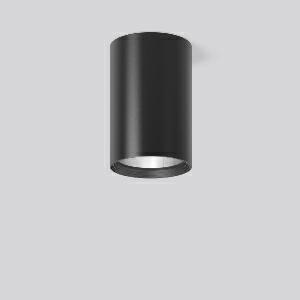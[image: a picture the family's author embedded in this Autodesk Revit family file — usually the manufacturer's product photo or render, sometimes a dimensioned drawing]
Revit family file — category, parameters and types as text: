
# Revit family: heledon_maxi_a_931223_003_76_2b7d
name_source: partatom
category: Lighting Fixtures
units: mm (PartAtom-declared; Revit-internal decimal feet)

## family parameters
Cut with Voids When Loaded = No
Host = Face
Light Source = No
Part Type = Normal
Room Calculation Point = No
Round Connector Dimension = Use Diameter
Shared = No

## types (1)
- HELEDON maxi A (1 x LED Modul 930, 4200 lm, 3000)
    Apparent Load = 35 VA
    Approval mark = CE
    CIE Flux Codes = 100 100 100 100 100
    Color Rendering = 90
    Color Temperature = 3000
    Default Elevation = 1800 mm
    Description = Series: HELEDON maxi
Cylindrical surface-mounted downlight. Housing: die-cast aluminium, powder-coated. Internal ceiling frame polycarbonate with bayonet mounting. Black plastic ring and recessed LED to prevent glare from the side. Optical assembly with reflector made of MIRO-Silver with 98% total light reflection for outstanding efficiency - can be changed without tools. Best colour rendering index Ra>90. Suitable for Ceiling mounting. Easy installation with a separate ceiling frame with bayonet mounting and plug connection. Driver integrated. Connected via plug-in connector. High quality converter without flickering and stroboscopic effect. The following accessories can be mounted without use of tools: interchangeable lenses, decorative glasses, honeycomb louvre, clear and frosted diffusers, white interchangeable plastic ring. 
Colour: deep black, matt (RAL 9005)
Diameter: 123 mm
Height: 183 mm
Lamp: LED
Socket: without socket
Colour temperature: 3000K
Colour rendering index (CRI): 92
System power: 35 W
Rated luminous flux: 4200 lm
Luminous efficiency: 120 lm/W
Control gear: Converter, dimmable, DALI
Protection class: I
Type of protection: IP 20
    Height = 183 mm
    Lamp = 1 x LED Modul 930
    Lamp Light Flux = 4200 lm
    Lamp count = 1
    Length = 123 mm
    Lifetime = 50000 h
    Luminous efficacy = 120 lm/W
    Manufacturer = RZB
    ModVariant = No
    Model = 931223.003.76
    Mounting Place = Ceiling
    Mounting Type = Surface mounted
    Number of Poles = 1
    OnlyDefault = Yes
    Power Factor = 1
    Product Name = HELEDON maxi A
    Product group = Surface mounted downlights
    ProductGroupID = 302
    Protection Class = Protection class I
    Protection Degree = IP 20
    RLX_Detail_Level = 1
    RLX_Emergency_Light_Flux = 0 lm
    RLX_Emergency_Type = 0
    RLX_Emergency_Type_DB = No
    RlxData = <blob elided: 97393 chars, md5=e8a95e8f>
    Socket = socket
    Standby Power = 0 W
    System Light Flux = 4200 lm
    System Power = 35 W
    Type Comments = Product without accessories
    Type Image = 931192.003.jpg
    URL = http://relux.com
    VarID = ---
    Voltage = 230 V
    Voltage Range = 220-240 V
    Weight = 0.00 kg
    Width = 0 mm  [stored 0 ft]

note: [stored X ft] marks values corroborated as IEEE doubles in the binary element streams (Revit-internal decimal feet)

## geometry (parser evidence)
native form markers: Blend x4, Sweep x9
no freeform markers — native parametric forms only
